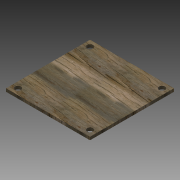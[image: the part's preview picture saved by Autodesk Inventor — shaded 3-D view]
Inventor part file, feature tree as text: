
AUTODESK INVENTOR PART (.ipt)
format: ipt  version: 2015 (Build 190159000, 159)  size: 103,424 bytes
history: native  units: in
note: dims shown in document units (in); Inventor stores cm internally (conversion verified against a paired STEP export)
features: extrude x1, sketch x1
ambient origin geometry x8: Origin, YZ Plane, XZ Plane, XY Plane, X Axis, Y Axis, Z Axis, Center Point
bodies: Solid1 (feature_tree)
feature tree (2):
  extrude  "Extrusion1"  Depth=7.0in
  sketch  "Sketch1"  dims[d0=7.0in d1=7.0in d2=0.25in d3=0.0in d4=0.5in d5=0.5in d6=0.5in d7=1.5748in d9=360.0deg]
